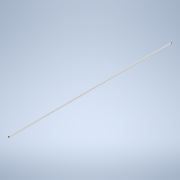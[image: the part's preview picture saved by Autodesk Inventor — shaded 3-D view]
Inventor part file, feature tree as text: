
AUTODESK INVENTOR PART (.ipt)
format: ipt  version: 2022 (Build 260153000, 153)  size: 90,624 bytes
history: native  units: in
note: dims shown in document units (in); Inventor stores cm internally (conversion verified against a paired STEP export)
features: extrude x1, sketch x1
ambient origin geometry x8: Origin, YZ Plane, XZ Plane, XY Plane, X Axis, Y Axis, Z Axis, Center Point
bodies: Solid1 (feature_tree)
feature tree (2):
  extrude  "Extrusion1"  Depth=6.5in TaperAngle=0.0deg
  sketch  "Sketch1"  dims[d0=0.05in d1=6.5in d2=0.0in]
